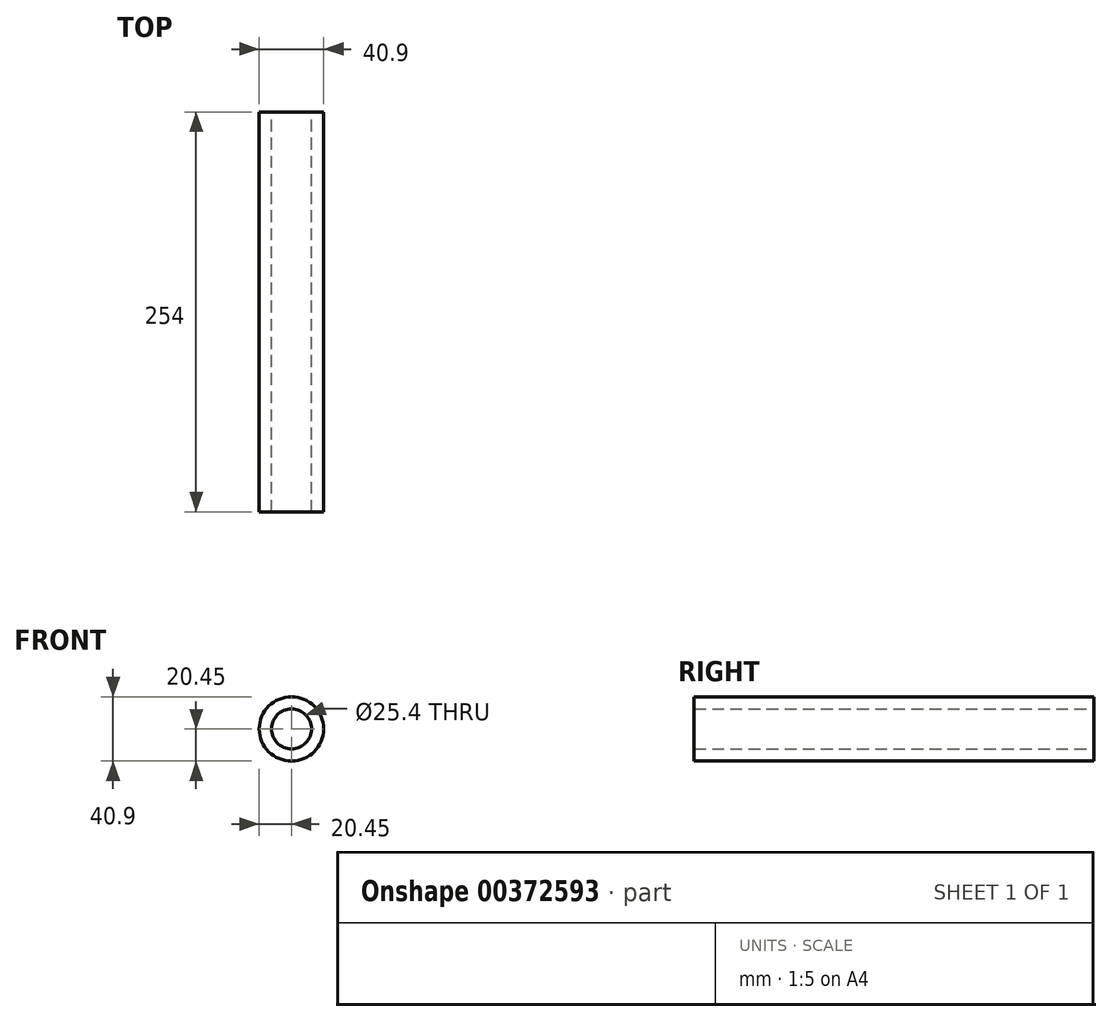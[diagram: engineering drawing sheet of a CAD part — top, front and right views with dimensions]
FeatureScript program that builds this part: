
annotation { "Feature Type Name" : "Feature", "Feature Type Description" : "" }
export const myFeature = defineFeature(function(context is Context, id is Id, definition is map)
    precondition{}
    {
        {
            var Q0;
            Q0=qCreatedBy(makeId("Front.planeOp"),FACE);
            var sketch = newSketch(context, id + "F0", { "sketchPlane" : qUnion([Q0])});
            skCircle(sketch, "E0", {"center": v(0, 0) * mm, "radius": 20.45 * mm});
            skSolve(sketch);
        }
        {
            var Q0;
            Q0=makeQuery(id+"F0.imprint","IMPRINT",FACE,{"disambiguationData":[TD([[makeQuery(id+"F0.imprint","IMPRINT",EDGE,{"derivedFrom":sQuery(id+"F0.wireOp",EDGE,"E0")}),1.0]])]});
            extrude(context, id + "F1", {"entities" : qUnion([Q0]), "depth" : 254 * mm});
        }
        {
            var Q0;
            Q0=sQuery(id+"F0.wireOp",VERTEX,"E0.center");
            var Q1;
            Q1=makeQuery(id+"F1.opExtrude","SWEPT_BODY",BODY,{"disambiguationData":[OSD([sQuery(id+"F0.wireOp",EDGE,"E0")])]});
            hole(context, id + "F2", {"style" : HoleStyle.C_BORE, "endStyle" : HoleEndStyle.THROUGH, "oppositeDirection" : true, "holeDiameter" : 25.4 * mm, "cBoreDiameter" : 25.4 * mm, "cBoreDepth" : 25.4 * mm, "isTappedThrough" : true, "tappedDepth" : 12.7 * mm, "tapClearance" : 3, "locations" : qUnion([Q0]), "scope" : qUnion([Q1])});
        }
    });
